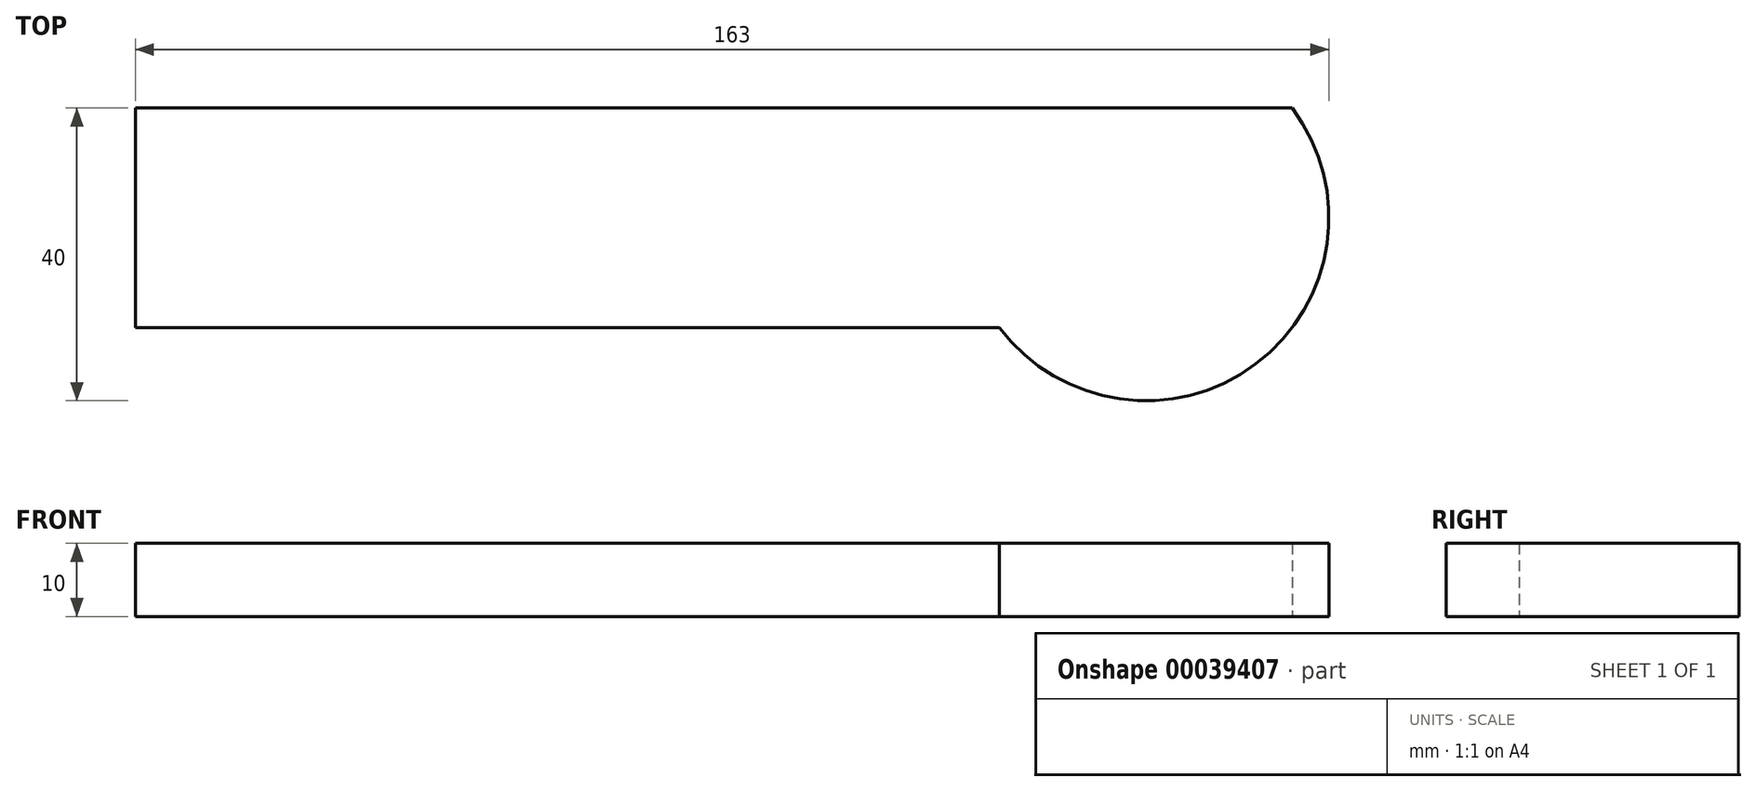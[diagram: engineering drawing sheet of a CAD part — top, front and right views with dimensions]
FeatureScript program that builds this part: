
annotation { "Feature Type Name" : "Feature", "Feature Type Description" : "" }
export const myFeature = defineFeature(function(context is Context, id is Id, definition is map)
    precondition{}
    {
        {
            var Q0;
            Q0=qCreatedBy(makeId("Top.planeOp"),FACE);
            var sketch = newSketch(context, id + "F0", { "sketchPlane" : qUnion([Q0])});
            skLineSegment(sketch, "E0.bottom", {"start": v(0, 0) * mm, "end": v(-118, 0) * mm});
            skLineSegment(sketch, "E0.top", {"start": v(0, 30) * mm, "end": v(-118, 30) * mm});
            skLineSegment(sketch, "E0.left", {"start": v(0, 0) * mm, "end": v(0, 30) * mm});
            skLineSegment(sketch, "E0.right", {"start": v(-118, 0) * mm, "end": v(-118, 30) * mm});
            skLineSegment(sketch, "E1", {"start": v(0, 30) * mm, "end": v(40, 30) * mm});
            skLineSegment(sketch, "E2", {"start": v(40, 30) * mm, "end": v(0, 0) * mm});
            skArc(sketch, "E3", {"start": v(0, 0) * mm, "mid": v(35, -5) * mm, "end": v(40, 30) * mm});
            skSolve(sketch);
        }
        {
            var Q0;
            Q0 = qSketchRegion(id + "F0", true);
            extrude(context, id + "F1", {"entities" : qUnion([Q0]), "depth" : 10 * mm});
        }
    });
